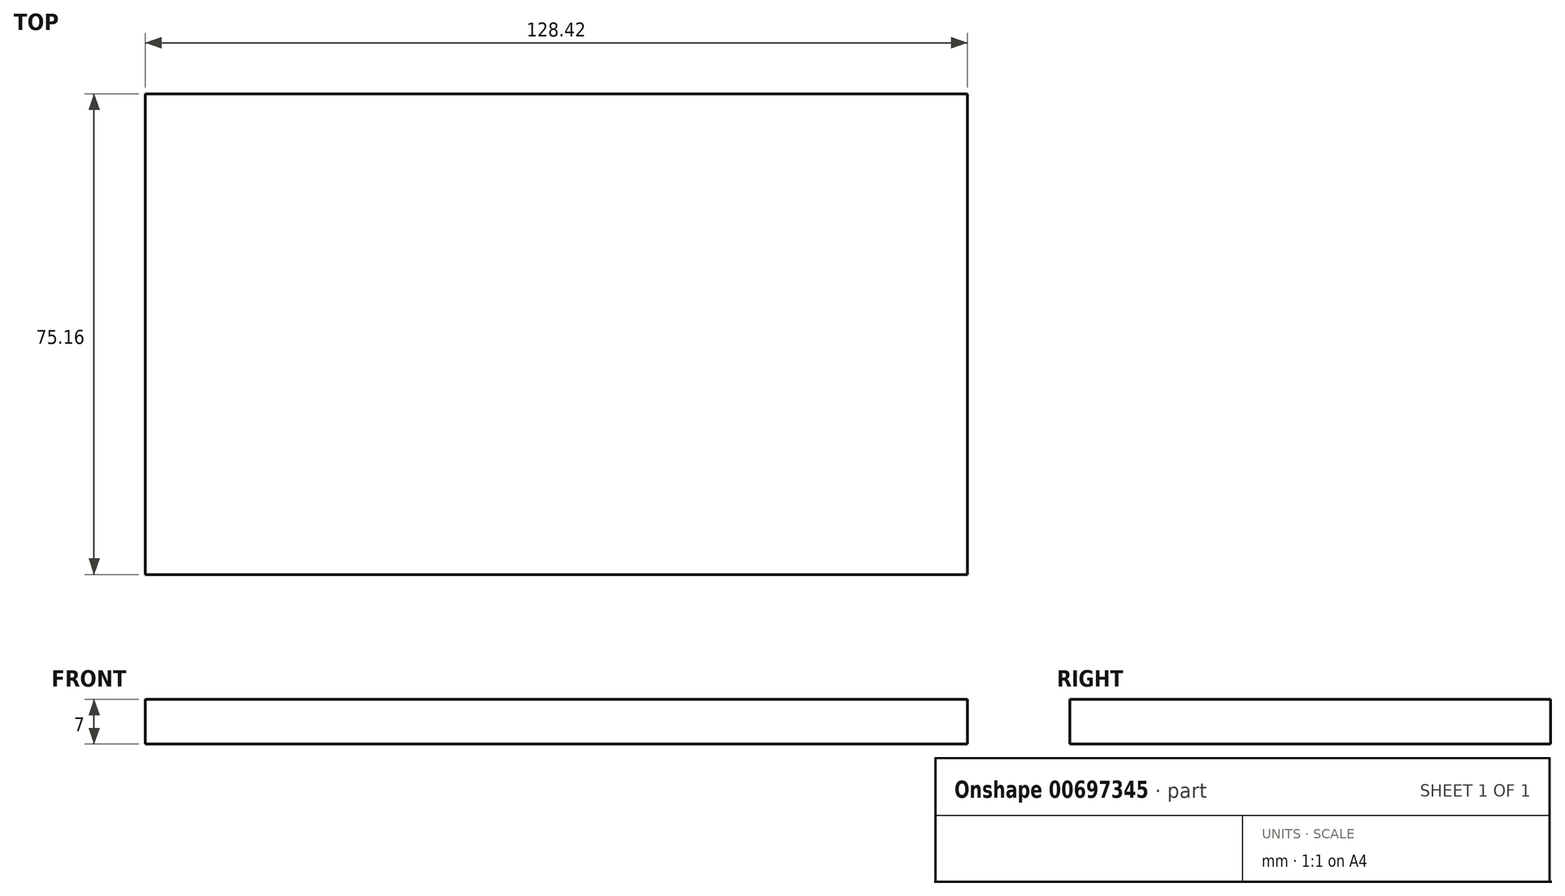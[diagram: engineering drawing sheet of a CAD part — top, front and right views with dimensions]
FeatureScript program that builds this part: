
annotation { "Feature Type Name" : "Feature", "Feature Type Description" : "" }
export const myFeature = defineFeature(function(context is Context, id is Id, definition is map)
    precondition{}
    {
        {
            var Q0;
            Q0=qCreatedBy(makeId("Top.planeOp"),FACE);
            var sketch = newSketch(context, id + "F0", { "sketchPlane" : qUnion([Q0])});
            skLineSegment(sketch, "E0.bottom", {"start": v(-53.6, 7.68) * mm, "end": v(74.82, 7.68) * mm});
            skLineSegment(sketch, "E0.top", {"start": v(-53.6, -67.48) * mm, "end": v(74.82, -67.48) * mm});
            skLineSegment(sketch, "E0.left", {"start": v(-53.6, 7.68) * mm, "end": v(-53.6, -67.48) * mm});
            skLineSegment(sketch, "E0.right", {"start": v(74.82, 7.68) * mm, "end": v(74.82, -67.48) * mm});
            skSolve(sketch);
        }
        {
            var Q0;
            Q0 = qSketchRegion(id + "F0", true);
            extrude(context, id + "F1", {"entities" : qUnion([Q0]), "depth" : 7 * mm, "offsetDistance" : 25 * mm});
        }
    });
